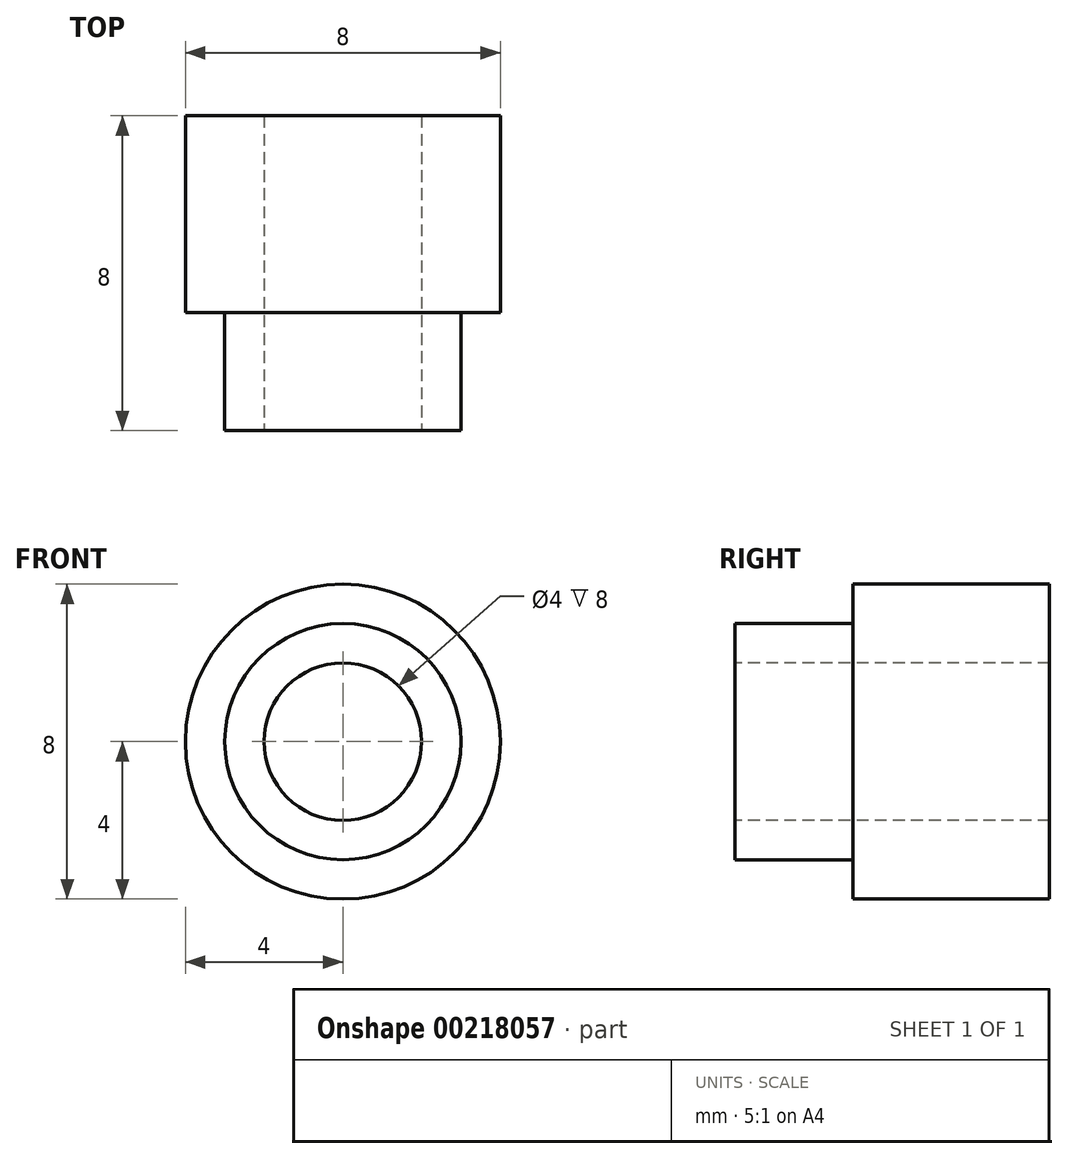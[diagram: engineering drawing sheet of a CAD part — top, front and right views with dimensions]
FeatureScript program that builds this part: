
annotation { "Feature Type Name" : "Feature", "Feature Type Description" : "" }
export const myFeature = defineFeature(function(context is Context, id is Id, definition is map)
    precondition{}
    {
        {
            var Q0;
            Q0=qCreatedBy(makeId("Front.planeOp"),FACE);
            var sketch = newSketch(context, id + "F0", { "sketchPlane" : qUnion([Q0])});
            skCircle(sketch, "E0", {"center": v(0, 0) * mm, "radius": 2 * mm});
            skCircle(sketch, "E1", {"center": v(0, 0) * mm, "radius": 3 * mm});
            skCircle(sketch, "E2", {"center": v(0, 0) * mm, "radius": 4 * mm});
            skSolve(sketch);
        }
        {
            var Q0;
            Q0=makeQuery(id+"F0.imprint","IMPRINT",FACE,{"disambiguationData":[TD([[makeQuery(id+"F0.imprint","IMPRINT",EDGE,{"derivedFrom":sQuery(id+"F0.wireOp",EDGE,"E0")}),-1.0]])]});
            extrude(context, id + "F1", {"entities" : qUnion([Q0]), "oppositeDirection" : true, "depth" : 5 * mm});
        }
        {
            var Q0;
            Q0=makeQuery(id+"F0.imprint","IMPRINT",FACE,{"disambiguationData":[TD([[makeQuery(id+"F0.imprint","IMPRINT",EDGE,{"derivedFrom":sQuery(id+"F0.wireOp",EDGE,"E1")}),-1.0]])]});
            extrude(context, id + "F2", {"entities" : qUnion([Q0]), "operationType" : NewBodyOperationType.ADD, "oppositeDirection" : true, "depth" : 5 * mm});
        }
        {
            var Q0;
            Q0=makeQuery(id+"F0.imprint","IMPRINT",FACE,{"disambiguationData":[TD([[makeQuery(id+"F0.imprint","IMPRINT",EDGE,{"derivedFrom":sQuery(id+"F0.wireOp",EDGE,"E0")}),-1.0]])]});
            extrude(context, id + "F3", {"entities" : qUnion([Q0]), "operationType" : NewBodyOperationType.ADD, "depth" : 3 * mm});
        }
    });
